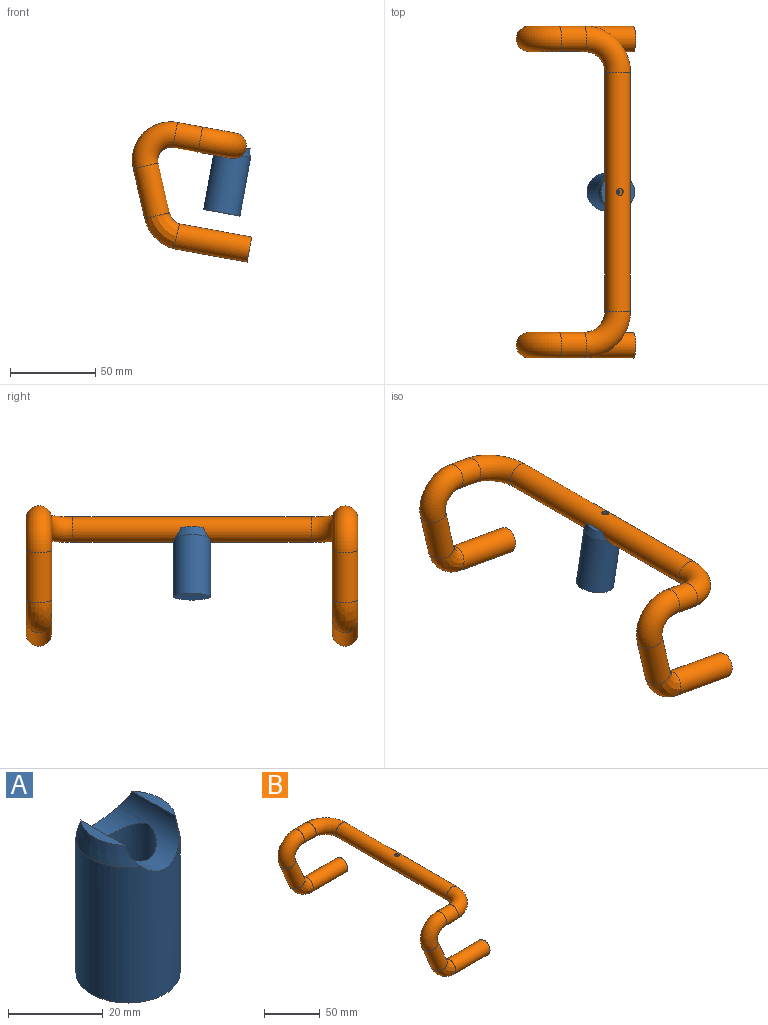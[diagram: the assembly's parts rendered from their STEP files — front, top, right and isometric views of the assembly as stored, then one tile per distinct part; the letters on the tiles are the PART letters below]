
ASSEMBLY  parts=2 mates=1
PART A: 9 faces, bbox 22x22x40 mm
  f0: plane 13.26x2.51mm, normal (0,0,1), area 22.8mm2, adj f4,f8
  f1: cylinder r=11mm len=35mm, axis (0,0,1), area 2377.8mm2, adj f2,f4,f7,f8
  f2: plane 22x22mm, normal (0,0,-1), area 380.1mm2, adj f1
  f3: plane 12.97x2.39mm, normal (0,0,1), area 21.2mm2, adj f4,f7
  f4: cylinder r=7.55mm len=22mm, axis (0,-1,0), area 313.8mm2, adj f0,f1,f3,f6,f7,f8
  f5: plane 12x12mm, normal (0,0,1), area 113.1mm2, adj f6
  f6: cylinder r=6mm len=30.5mm, axis (0,0,1), area 1087.4mm2, adj f4,f5
  f7: cone r=10mm half-angle=11.3deg, axis (0,0,-1), area 89.4mm2, adj f1,f3,f4
  f8: cone r=10mm half-angle=11.3deg, axis (0,0,-1), area 91.1mm2, adj f0,f1,f4
PART B: 28 faces, bbox 79.4x210x75.3 mm
  f0: cylinder r=7.5mm len=140mm, axis (0,1,0), area 6572mm2, adj f7,f19,f26,f27
  f1: cylinder r=6.5mm len=140mm, axis (0,1,0), area 5692.3mm2, adj f12,f24,f26,f27
  f2: plane 15x15mm, normal (1,0,0), area 44mm2, adj f8,f13
  f3: bspline ~30x21.63mm, area 822.7mm2, adj f4,f8
  f4: cylinder r=7.5mm len=33.49mm, axis (-0.39,0,0.92), area 1413.7mm2, adj f3,f5
  f5: torus R=15mm, axis (0,1,0), area 1397.3mm2, adj f4,f6
  f6: cylinder r=7.5mm len=15mm, axis (1,0,0), area 706.9mm2, adj f5,f7
  f7: torus R=20mm, axis (0,0,1), area 1480.4mm2, adj f0,f6
  f8: cylinder r=7.5mm len=44.07mm, axis (-1,0,0), area 2061.5mm2, adj f2,f3
  f9: cylinder r=6.5mm len=32.7mm, axis (-0.39,0,0.92), area 1225.2mm2, adj f10
  f10: torus R=15mm, axis (0,1,0), area 1211mm2, adj f9,f11
  f11: cylinder r=6.5mm len=15mm, axis (1,0,0), area 612.6mm2, adj f10,f12
  f12: torus R=20mm, axis (0,0,1), area 1283mm2, adj f1,f11
  f13: cylinder r=6.5mm len=43.64mm, axis (-1,0,0), area 1782.2mm2, adj f2
  f14: plane 15x15mm, normal (1,0,0), area 44mm2, adj f20,f25
  f15: bspline ~30x21.63mm, area 822.7mm2, adj f16,f20
  f16: cylinder r=7.5mm len=33.49mm, axis (-0.39,0,0.92), area 1413.7mm2, adj f15,f17
  f17: torus R=15mm, axis (0,-1,0), area 1397.3mm2, adj f16,f18
  f18: cylinder r=7.5mm len=15mm, axis (1,0,0), area 706.9mm2, adj f17,f19
  f19: torus R=20mm, axis (0,0,1), area 1480.4mm2, adj f0,f18
  f20: cylinder r=7.5mm len=44.07mm, axis (-1,0,0), area 2061.5mm2, adj f14,f15
  f21: cylinder r=6.5mm len=32.7mm, axis (-0.39,0,0.92), area 1225.2mm2, adj f22
  f22: torus R=15mm, axis (0,-1,0), area 1211mm2, adj f21,f23
  f23: cylinder r=6.5mm len=15mm, axis (1,0,0), area 612.6mm2, adj f22,f24
  f24: torus R=20mm, axis (0,0,1), area 1283mm2, adj f1,f23
  f25: cylinder r=6.5mm len=43.64mm, axis (-1,0,0), area 1782.2mm2, adj f14
  f26: cylinder r=2mm len=4mm, axis (0,0,-1), area 13.1mm2, adj f0,f1
  f27: cylinder r=2mm len=4mm, axis (0,0,-1), area 12.6mm2, adj f0,f1
PLACE A rot(axis=(0,1,0),10.3deg) t=(-34.13,12.8,2.52)mm
PLACE B rot(axis=(0,1,0),10.3deg) t=(25.74,12.8,-8.37)mm
MATE fastened A.f1 <-> B.f26  axis (0.18,0,0.98) through (24.84,12.8,-13.3)mm
